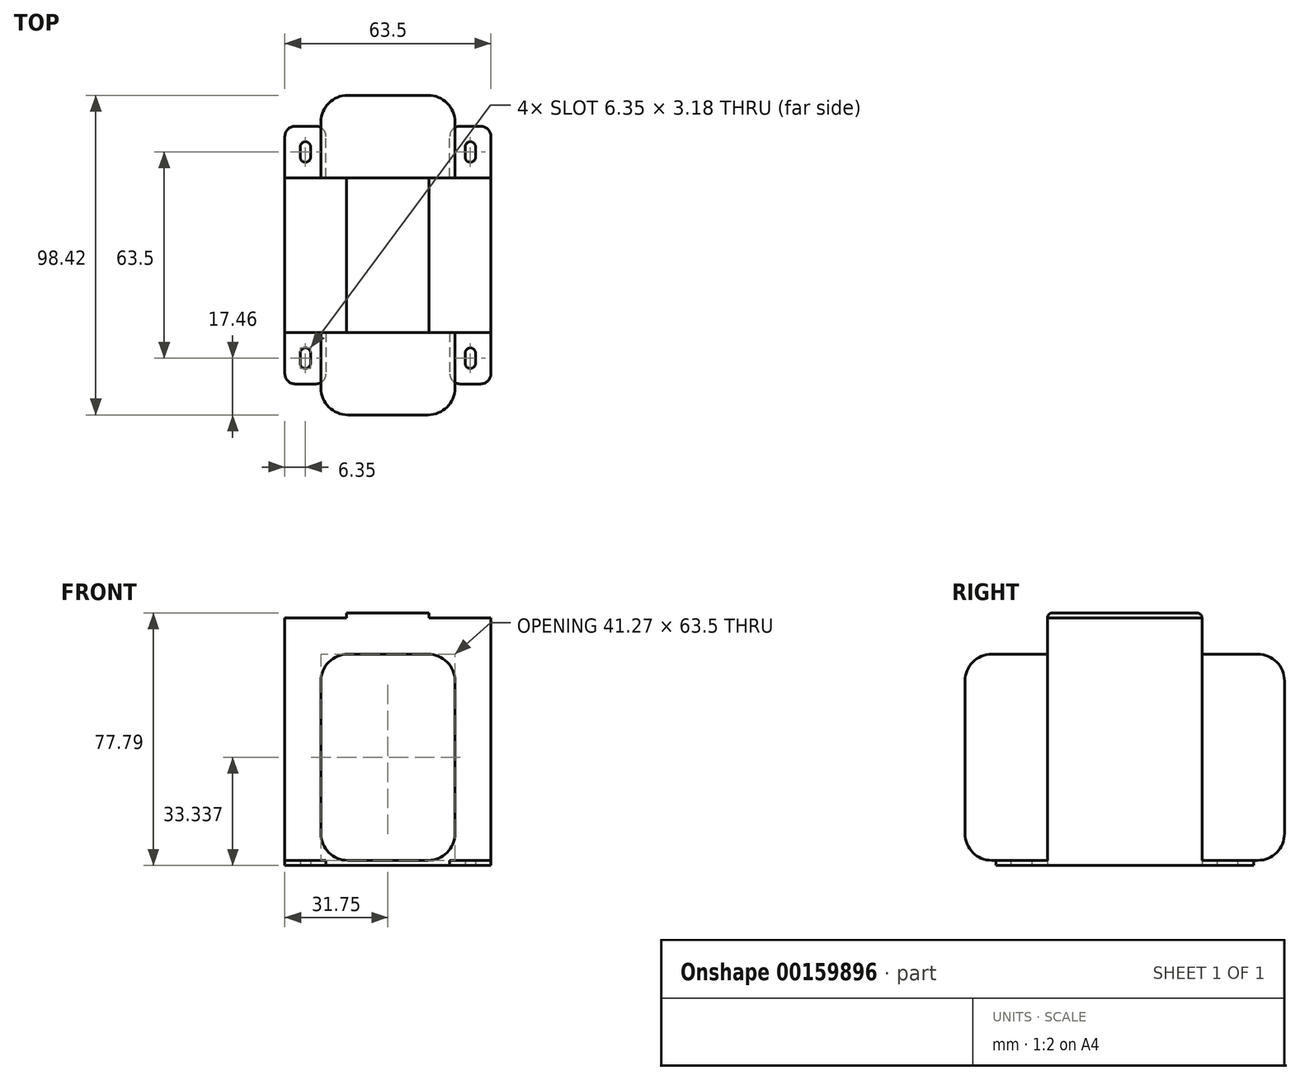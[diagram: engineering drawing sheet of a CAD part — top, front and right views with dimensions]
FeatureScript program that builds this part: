
annotation { "Feature Type Name" : "Feature", "Feature Type Description" : "" }
export const myFeature = defineFeature(function(context is Context, id is Id, definition is map)
    precondition{}
    {
        {
            var Q0;
            Q0=qCreatedBy(makeId("Top.planeOp"),FACE);
            var sketch = newSketch(context, id + "F0", { "sketchPlane" : qUnion([Q0])});
            skLineSegment(sketch, "E0.bottom", {"start": v(31.75, -23.81) * mm, "end": v(-31.75, -23.81) * mm});
            skLineSegment(sketch, "E0.top", {"start": v(31.75, 23.81) * mm, "end": v(-31.75, 23.81) * mm});
            skLineSegment(sketch, "E0.left", {"start": v(31.75, -23.81) * mm, "end": v(31.75, 23.81) * mm});
            skLineSegment(sketch, "E0.right", {"start": v(-31.75, -23.81) * mm, "end": v(-31.75, 23.81) * mm});
            skPoint(sketch, "E0.middle", {"position": v(0, 0) * mm});
            skSolve(sketch);
        }
        {
            var Q0;
            Q0=makeQuery(id+"F0.imprint","IMPRINT",FACE,{"disambiguationData":[TD([[makeQuery(id+"F0.imprint","IMPRINT",EDGE,{"derivedFrom":sQuery(id+"F0.wireOp",EDGE,"E0.bottom")}),-1.0]])]});
            extrude(context, id + "F1", {"entities" : qUnion([Q0]), "depth" : 76.2 * mm});
        }
        {
            var Q0;
            Q0=makeQuery(id+"F1.opExtrude","SWEPT_FACE",FACE,{"disambiguationData":[OSD([sQuery(id+"F0.wireOp",EDGE,"E0.bottom")])]});
            var sketch = newSketch(context, id + "F2", { "sketchPlane" : qUnion([Q0])});
            skLineSegment(sketch, "E1.bottom", {"start": v(-20.64, 65.09) * mm, "end": v(20.64, 65.09) * mm});
            skLineSegment(sketch, "E1.top", {"start": v(-20.64, 1.59) * mm, "end": v(20.64, 1.59) * mm});
            skLineSegment(sketch, "E1.left", {"start": v(-20.64, 65.09) * mm, "end": v(-20.64, 1.59) * mm});
            skLineSegment(sketch, "E1.right", {"start": v(20.64, 65.09) * mm, "end": v(20.64, 1.59) * mm});
            skSolve(sketch);
        }
        {
            var Q0;
            Q0=makeQuery(id+"F2.imprint","IMPRINT",FACE,{"disambiguationData":[TD([[makeQuery(id+"F2.imprint","IMPRINT",EDGE,{"derivedFrom":sQuery(id+"F2.wireOp",EDGE,"E1.bottom")}),-1.0]])]});
            extrude(context, id + "F3", {"entities" : qUnion([Q0]), "depth" : 25.4 * mm});
        }
        {
            var Q0;
            Q0=makeQuery(id+"F3.opExtrude","SWEPT_EDGE",EDGE,{"disambiguationData":[OSD([sQuery(id+"F2.wireOp",EDGE,"E1.bottom"),sQuery(id+"F2.wireOp",EDGE,"E1.left")])]});
            var Q1;
            Q1=makeQuery(id+"F3.opExtrude","SWEPT_EDGE",EDGE,{"disambiguationData":[OSD([sQuery(id+"F2.wireOp",EDGE,"E1.bottom"),sQuery(id+"F2.wireOp",EDGE,"E1.right")])]});
            var Q2;
            Q2=makeQuery(id+"F3.opExtrude","SWEPT_EDGE",EDGE,{"disambiguationData":[OSD([sQuery(id+"F0.wireOp",EDGE,"E0.bottom"),sQuery(id+"F2.wireOp",EDGE,"E1.top"),sQuery(id+"F2.wireOp",EDGE,"E1.left")])]});
            var Q3;
            Q3=makeQuery(id+"F3.opExtrude","SWEPT_EDGE",EDGE,{"disambiguationData":[OSD([sQuery(id+"F0.wireOp",EDGE,"E0.bottom"),sQuery(id+"F2.wireOp",EDGE,"E1.top"),sQuery(id+"F2.wireOp",EDGE,"E1.right")])]});
            var Q4;
            Q4=makeQuery(id+"F3.opExtrude","CAP_EDGE",EDGE,{"disambiguationData":[OSD([sQuery(id+"F2.wireOp",EDGE,"E1.right")])],"isStart":false});
            var Q5;
            Q5=makeQuery(id+"F3.opExtrude","CAP_FACE",FACE,{"disambiguationData":[OSD([sQuery(id+"F2.wireOp",EDGE,"E1.bottom"),sQuery(id+"F2.wireOp",EDGE,"E1.top"),sQuery(id+"F2.wireOp",EDGE,"E1.left"),sQuery(id+"F2.wireOp",EDGE,"E1.right")])],"isStart":false});
            fillet(context, id + "F4", {"entities" : qUnion([Q0, Q1, Q2, Q3, Q4, Q5]), "radius" : 8.25 * mm, "tangentPropagation" : true, "allowEdgeOverflow" : false});
        }
        {
            var Q0;
            Q0=makeQuery(id+"F3.opExtrude","SWEPT_BODY",BODY,{"disambiguationData":[OSD([sQuery(id+"F2.wireOp",EDGE,"E1.bottom"),sQuery(id+"F2.wireOp",EDGE,"E1.top"),sQuery(id+"F2.wireOp",EDGE,"E1.left"),sQuery(id+"F2.wireOp",EDGE,"E1.right")])]});
            var Q1;
            Q1=qCreatedBy(makeId("Front.planeOp"),FACE);
            mirror(context, id + "F5", {"operationType" : NewBodyOperationType.ADD, "entities" : qUnion([Q0]), "mirrorPlane" : qUnion([Q1])});
        }
        {
            var Q0;
            {var subQ0=makeQuery(id+"F3.opExtrude","SWEPT_FACE",FACE,{"disambiguationData":[OSD([sQuery(id+"F2.wireOp",EDGE,"E1.top")])]});Q0=makeQuery(id+"F5.boolean.opBoolean","MERGE",FACE,{"derivedFrom":[makeQuery(id+"F1.opExtrude","CAP_FACE",FACE,{"disambiguationData":[OSD([sQuery(id+"F0.wireOp",EDGE,"E0.bottom"),sQuery(id+"F0.wireOp",EDGE,"E0.top"),sQuery(id+"F0.wireOp",EDGE,"E0.left"),sQuery(id+"F0.wireOp",EDGE,"E0.right")])],"isStart":true}),subQ0,makeQuery(id+"F5.opPattern","COPY",FACE,{"derivedFrom":subQ0,"instanceName":"1"})]});}
            var sketch = newSketch(context, id + "F6", { "sketchPlane" : qUnion([Q0])});
            skLineSegment(sketch, "E2.bottom", {"start": v(-31.75, 23.81) * mm, "end": v(-19.05, 23.81) * mm});
            skLineSegment(sketch, "E2.top", {"start": v(-31.75, 39.69) * mm, "end": v(-19.05, 39.69) * mm});
            skLineSegment(sketch, "E2.left", {"start": v(-31.75, 23.81) * mm, "end": v(-31.75, 39.69) * mm});
            skLineSegment(sketch, "E2.right", {"start": v(-19.05, 23.81) * mm, "end": v(-19.05, 39.69) * mm});
            skLineSegment(sketch, "E3.MirrorCS", {"start": v(31.75, 23.81) * mm, "end": v(19.05, 23.81) * mm});
            skLineSegment(sketch, "E4.MirrorCS", {"start": v(19.05, 23.81) * mm, "end": v(19.05, 39.69) * mm});
            skLineSegment(sketch, "E5.MirrorCS", {"start": v(31.75, 23.81) * mm, "end": v(31.75, 39.69) * mm});
            skLineSegment(sketch, "E6.MirrorCS", {"start": v(31.75, 39.69) * mm, "end": v(19.05, 39.69) * mm});
            skLineSegment(sketch, "E7.MirrorCS", {"start": v(31.75, -23.81) * mm, "end": v(19.05, -23.81) * mm});
            skLineSegment(sketch, "E8.MirrorCS", {"start": v(31.75, -23.81) * mm, "end": v(31.75, -39.69) * mm});
            skLineSegment(sketch, "E9.MirrorCS", {"start": v(31.75, -39.69) * mm, "end": v(19.05, -39.69) * mm});
            skLineSegment(sketch, "E10.MirrorCS", {"start": v(19.05, -23.81) * mm, "end": v(19.05, -39.69) * mm});
            skLineSegment(sketch, "E11.MirrorCS", {"start": v(-31.75, -39.69) * mm, "end": v(-19.05, -39.69) * mm});
            skLineSegment(sketch, "E12.MirrorCS", {"start": v(-19.05, -23.81) * mm, "end": v(-19.05, -39.69) * mm});
            skLineSegment(sketch, "E13.MirrorCS", {"start": v(-31.75, -23.81) * mm, "end": v(-31.75, -39.69) * mm});
            skLineSegment(sketch, "E14.MirrorCS", {"start": v(-31.75, -23.81) * mm, "end": v(-19.05, -23.81) * mm});
            skSolve(sketch);
        }
        {
            var Q0;
            Q0=makeQuery(id+"F6.imprint","IMPRINT",FACE,{"disambiguationData":[TD([[makeQuery(id+"F6.imprint","IMPRINT",EDGE,{"derivedFrom":sQuery(id+"F6.wireOp",EDGE,"E2.bottom")}),-1.0]])]});
            var Q1;
            Q1=makeQuery(id+"F6.imprint","IMPRINT",FACE,{"disambiguationData":[TD([[makeQuery(id+"F6.imprint","IMPRINT",EDGE,{"derivedFrom":sQuery(id+"F6.wireOp",EDGE,"E3.MirrorCS")}),-1.0]])]});
            var Q2;
            Q2=makeQuery(id+"F6.imprint","IMPRINT",FACE,{"disambiguationData":[TD([[makeQuery(id+"F6.imprint","IMPRINT",EDGE,{"derivedFrom":sQuery(id+"F6.wireOp",EDGE,"E7.MirrorCS")}),1.0]])]});
            var Q3;
            Q3=makeQuery(id+"F6.imprint","IMPRINT",FACE,{"disambiguationData":[TD([[makeQuery(id+"F6.imprint","IMPRINT",EDGE,{"derivedFrom":sQuery(id+"F6.wireOp",EDGE,"E11.MirrorCS")}),1.0]])]});
            extrude(context, id + "F7", {"entities" : qUnion([Q0, Q1, Q2, Q3]), "operationType" : NewBodyOperationType.ADD, "oppositeDirection" : true, "depth" : 1.59 * mm});
        }
        {
            var Q0;
            Q0=makeQuery(id+"F7.opExtrude","SWEPT_EDGE",EDGE,{"disambiguationData":[OSD([sQuery(id+"F6.wireOp",EDGE,"E2.top"),sQuery(id+"F6.wireOp",EDGE,"E2.left")])]});
            var Q1;
            Q1=makeQuery(id+"F7.opExtrude","SWEPT_EDGE",EDGE,{"disambiguationData":[OSD([sQuery(id+"F6.wireOp",EDGE,"E2.top"),sQuery(id+"F6.wireOp",EDGE,"E2.right")])]});
            var Q2;
            Q2=makeQuery(id+"F7.opExtrude","SWEPT_EDGE",EDGE,{"disambiguationData":[OSD([sQuery(id+"F6.wireOp",EDGE,"E4.MirrorCS"),sQuery(id+"F6.wireOp",EDGE,"E6.MirrorCS")])]});
            var Q3;
            Q3=makeQuery(id+"F7.opExtrude","SWEPT_EDGE",EDGE,{"disambiguationData":[OSD([sQuery(id+"F6.wireOp",EDGE,"E5.MirrorCS"),sQuery(id+"F6.wireOp",EDGE,"E6.MirrorCS")])]});
            var Q4;
            Q4=makeQuery(id+"F7.opExtrude","SWEPT_EDGE",EDGE,{"disambiguationData":[OSD([sQuery(id+"F6.wireOp",EDGE,"E8.MirrorCS"),sQuery(id+"F6.wireOp",EDGE,"E9.MirrorCS")])]});
            var Q5;
            Q5=makeQuery(id+"F7.opExtrude","SWEPT_EDGE",EDGE,{"disambiguationData":[OSD([sQuery(id+"F6.wireOp",EDGE,"E9.MirrorCS"),sQuery(id+"F6.wireOp",EDGE,"E10.MirrorCS")])]});
            var Q6;
            Q6=makeQuery(id+"F7.opExtrude","SWEPT_EDGE",EDGE,{"disambiguationData":[OSD([sQuery(id+"F6.wireOp",EDGE,"E11.MirrorCS"),sQuery(id+"F6.wireOp",EDGE,"E12.MirrorCS")])]});
            var Q7;
            Q7=makeQuery(id+"F7.opExtrude","SWEPT_EDGE",EDGE,{"disambiguationData":[OSD([sQuery(id+"F6.wireOp",EDGE,"E11.MirrorCS"),sQuery(id+"F6.wireOp",EDGE,"E13.MirrorCS")])]});
            fillet(context, id + "F8", {"entities" : qUnion([Q0, Q1, Q2, Q3, Q4, Q5, Q6, Q7]), "radius" : 3.17 * mm, "tangentPropagation" : true, "allowEdgeOverflow" : false});
        }
        {
            var Q0;
            Q0=makeQuery(id+"F7.boolean.opBoolean","MERGE",FACE,{"derivedFrom":[makeQuery(id+"F1.opExtrude","CAP_FACE",FACE,{"disambiguationData":[OSD([sQuery(id+"F0.wireOp",EDGE,"E0.bottom"),sQuery(id+"F0.wireOp",EDGE,"E0.top"),sQuery(id+"F0.wireOp",EDGE,"E0.left"),sQuery(id+"F0.wireOp",EDGE,"E0.right")])],"isStart":true}),makeQuery(id+"F7.opExtrude","CAP_FACE",FACE,{"disambiguationData":[OSD([sQuery(id+"F6.wireOp",EDGE,"E2.bottom"),sQuery(id+"F6.wireOp",EDGE,"E2.top"),sQuery(id+"F6.wireOp",EDGE,"E2.left"),sQuery(id+"F6.wireOp",EDGE,"E2.right")])],"isStart":true}),makeQuery(id+"F7.opExtrude","CAP_FACE",FACE,{"disambiguationData":[OSD([sQuery(id+"F6.wireOp",EDGE,"E3.MirrorCS"),sQuery(id+"F6.wireOp",EDGE,"E4.MirrorCS"),sQuery(id+"F6.wireOp",EDGE,"E5.MirrorCS"),sQuery(id+"F6.wireOp",EDGE,"E6.MirrorCS")])],"isStart":true}),makeQuery(id+"F7.opExtrude","CAP_FACE",FACE,{"disambiguationData":[OSD([sQuery(id+"F6.wireOp",EDGE,"E7.MirrorCS"),sQuery(id+"F6.wireOp",EDGE,"E8.MirrorCS"),sQuery(id+"F6.wireOp",EDGE,"E9.MirrorCS"),sQuery(id+"F6.wireOp",EDGE,"E10.MirrorCS")])],"isStart":true}),makeQuery(id+"F7.opExtrude","CAP_FACE",FACE,{"disambiguationData":[OSD([sQuery(id+"F6.wireOp",EDGE,"E11.MirrorCS"),sQuery(id+"F6.wireOp",EDGE,"E12.MirrorCS"),sQuery(id+"F6.wireOp",EDGE,"E13.MirrorCS"),sQuery(id+"F6.wireOp",EDGE,"E14.MirrorCS")])],"isStart":true})]});
            var sketch = newSketch(context, id + "F9", { "sketchPlane" : qUnion([Q0])});
            skLineSegment(sketch, "E15", {"start": v(-25.4, 39.69) * mm, "end": v(-25.4, 23.81) * mm, "construction": true});
            skLineSegment(sketch, "E16", {"start": v(-31.75, 31.75) * mm, "end": v(-19.05, 31.75) * mm, "construction": true});
            skPoint(sketch, "E16.startSnap0", {"position": v(-25.4, 31.75) * mm});
            skLineSegment(sketch, "E17.bottom", {"start": v(-26.99, 28.58) * mm, "end": v(-23.81, 28.58) * mm});
            skLineSegment(sketch, "E17.top", {"start": v(-26.99, 34.93) * mm, "end": v(-23.81, 34.93) * mm});
            skLineSegment(sketch, "E17.left", {"start": v(-26.99, 28.58) * mm, "end": v(-26.99, 34.93) * mm});
            skLineSegment(sketch, "E17.right", {"start": v(-23.81, 28.58) * mm, "end": v(-23.81, 34.93) * mm});
            skLineSegment(sketch, "E18.MirrorCS", {"start": v(26.99, 34.93) * mm, "end": v(23.81, 34.93) * mm});
            skLineSegment(sketch, "E19.MirrorCS", {"start": v(23.81, 28.58) * mm, "end": v(23.81, 34.93) * mm});
            skLineSegment(sketch, "E20.MirrorCS", {"start": v(26.99, 28.58) * mm, "end": v(26.99, 34.93) * mm});
            skLineSegment(sketch, "E21.MirrorCS", {"start": v(26.99, 28.58) * mm, "end": v(23.81, 28.58) * mm});
            skLineSegment(sketch, "E22.MirrorCS", {"start": v(26.99, -28.58) * mm, "end": v(23.81, -28.58) * mm});
            skLineSegment(sketch, "E23.MirrorCS", {"start": v(26.99, -28.58) * mm, "end": v(26.99, -34.93) * mm});
            skLineSegment(sketch, "E24.MirrorCS", {"start": v(26.99, -34.93) * mm, "end": v(23.81, -34.93) * mm});
            skLineSegment(sketch, "E25.MirrorCS", {"start": v(23.81, -28.58) * mm, "end": v(23.81, -34.93) * mm});
            skLineSegment(sketch, "E26.MirrorCS", {"start": v(-26.99, -28.58) * mm, "end": v(-23.81, -28.58) * mm});
            skLineSegment(sketch, "E27.MirrorCS", {"start": v(-26.99, -34.93) * mm, "end": v(-23.81, -34.93) * mm});
            skLineSegment(sketch, "E28.MirrorCS", {"start": v(-26.99, -28.58) * mm, "end": v(-26.99, -34.93) * mm});
            skLineSegment(sketch, "E29.MirrorCS", {"start": v(-23.81, -28.58) * mm, "end": v(-23.81, -34.93) * mm});
            skSolve(sketch);
        }
        {
            var Q0;
            Q0=makeQuery(id+"F9.imprint","IMPRINT",FACE,{"disambiguationData":[TD([[makeQuery(id+"F9.imprint","IMPRINT",EDGE,{"derivedFrom":sQuery(id+"F9.wireOp",EDGE,"E17.bottom")}),1.0]])]});
            var Q1;
            Q1=makeQuery(id+"F9.imprint","IMPRINT",FACE,{"disambiguationData":[TD([[makeQuery(id+"F9.imprint","IMPRINT",EDGE,{"derivedFrom":sQuery(id+"F9.wireOp",EDGE,"E18.MirrorCS")}),1.0]])]});
            var Q2;
            Q2=makeQuery(id+"F9.imprint","IMPRINT",FACE,{"disambiguationData":[TD([[makeQuery(id+"F9.imprint","IMPRINT",EDGE,{"derivedFrom":sQuery(id+"F9.wireOp",EDGE,"E22.MirrorCS")}),1.0]])]});
            var Q3;
            Q3=makeQuery(id+"F9.imprint","IMPRINT",FACE,{"disambiguationData":[TD([[makeQuery(id+"F9.imprint","IMPRINT",EDGE,{"derivedFrom":sQuery(id+"F9.wireOp",EDGE,"E26.MirrorCS")}),-1.0]])]});
            extrude(context, id + "F10", {"entities" : qUnion([Q0, Q1, Q2, Q3]), "operationType" : NewBodyOperationType.REMOVE, "oppositeDirection" : true, "depth" : 25.4 * mm});
        }
        {
            var Q0;
            Q0=makeQuery(id+"F10.boolean.opBoolean","COPY",EDGE,{"derivedFrom":makeQuery(id+"F10.opExtrude","SWEPT_EDGE",EDGE,{"disambiguationData":[OSD([sQuery(id+"F9.wireOp",EDGE,"E17.top"),sQuery(id+"F9.wireOp",EDGE,"E17.left")])]})});
            var Q1;
            Q1=makeQuery(id+"F10.boolean.opBoolean","COPY",EDGE,{"derivedFrom":makeQuery(id+"F10.opExtrude","SWEPT_EDGE",EDGE,{"disambiguationData":[OSD([sQuery(id+"F9.wireOp",EDGE,"E17.top"),sQuery(id+"F9.wireOp",EDGE,"E17.right")])]})});
            var Q2;
            Q2=makeQuery(id+"F10.boolean.opBoolean","COPY",EDGE,{"derivedFrom":makeQuery(id+"F10.opExtrude","SWEPT_EDGE",EDGE,{"disambiguationData":[OSD([sQuery(id+"F9.wireOp",EDGE,"E17.bottom"),sQuery(id+"F9.wireOp",EDGE,"E17.left")])]})});
            var Q3;
            Q3=makeQuery(id+"F10.boolean.opBoolean","COPY",EDGE,{"derivedFrom":makeQuery(id+"F10.opExtrude","SWEPT_EDGE",EDGE,{"disambiguationData":[OSD([sQuery(id+"F9.wireOp",EDGE,"E17.bottom"),sQuery(id+"F9.wireOp",EDGE,"E17.right")])]})});
            var Q4;
            Q4=makeQuery(id+"F10.boolean.opBoolean","COPY",EDGE,{"derivedFrom":makeQuery(id+"F10.opExtrude","SWEPT_EDGE",EDGE,{"disambiguationData":[OSD([sQuery(id+"F9.wireOp",EDGE,"E21.MirrorCS"),sQuery(id+"F9.wireOp",EDGE,"E20.MirrorCS")])]})});
            var Q5;
            Q5=makeQuery(id+"F10.boolean.opBoolean","COPY",EDGE,{"derivedFrom":makeQuery(id+"F10.opExtrude","SWEPT_EDGE",EDGE,{"disambiguationData":[OSD([sQuery(id+"F9.wireOp",EDGE,"E18.MirrorCS"),sQuery(id+"F9.wireOp",EDGE,"E20.MirrorCS")])]})});
            var Q6;
            Q6=makeQuery(id+"F10.boolean.opBoolean","COPY",EDGE,{"derivedFrom":makeQuery(id+"F10.opExtrude","SWEPT_EDGE",EDGE,{"disambiguationData":[OSD([sQuery(id+"F9.wireOp",EDGE,"E18.MirrorCS"),sQuery(id+"F9.wireOp",EDGE,"E19.MirrorCS")])]})});
            var Q7;
            Q7=makeQuery(id+"F10.boolean.opBoolean","COPY",EDGE,{"derivedFrom":makeQuery(id+"F10.opExtrude","SWEPT_EDGE",EDGE,{"disambiguationData":[OSD([sQuery(id+"F9.wireOp",EDGE,"E19.MirrorCS"),sQuery(id+"F9.wireOp",EDGE,"E21.MirrorCS")])]})});
            var Q8;
            Q8=makeQuery(id+"F10.boolean.opBoolean","COPY",EDGE,{"derivedFrom":makeQuery(id+"F10.opExtrude","SWEPT_EDGE",EDGE,{"disambiguationData":[OSD([sQuery(id+"F9.wireOp",EDGE,"E27.MirrorCS"),sQuery(id+"F9.wireOp",EDGE,"E28.MirrorCS")])]})});
            var Q9;
            Q9=makeQuery(id+"F10.boolean.opBoolean","COPY",EDGE,{"derivedFrom":makeQuery(id+"F10.opExtrude","SWEPT_EDGE",EDGE,{"disambiguationData":[OSD([sQuery(id+"F9.wireOp",EDGE,"E27.MirrorCS"),sQuery(id+"F9.wireOp",EDGE,"E29.MirrorCS")])]})});
            var Q10;
            Q10=makeQuery(id+"F10.boolean.opBoolean","COPY",EDGE,{"derivedFrom":makeQuery(id+"F10.opExtrude","SWEPT_EDGE",EDGE,{"disambiguationData":[OSD([sQuery(id+"F9.wireOp",EDGE,"E26.MirrorCS"),sQuery(id+"F9.wireOp",EDGE,"E29.MirrorCS")])]})});
            var Q11;
            Q11=makeQuery(id+"F10.boolean.opBoolean","COPY",EDGE,{"derivedFrom":makeQuery(id+"F10.opExtrude","SWEPT_EDGE",EDGE,{"disambiguationData":[OSD([sQuery(id+"F9.wireOp",EDGE,"E26.MirrorCS"),sQuery(id+"F9.wireOp",EDGE,"E28.MirrorCS")])]})});
            var Q12;
            Q12=makeQuery(id+"F10.boolean.opBoolean","COPY",EDGE,{"derivedFrom":makeQuery(id+"F10.opExtrude","SWEPT_EDGE",EDGE,{"disambiguationData":[OSD([sQuery(id+"F9.wireOp",EDGE,"E22.MirrorCS"),sQuery(id+"F9.wireOp",EDGE,"E25.MirrorCS")])]})});
            var Q13;
            Q13=makeQuery(id+"F10.boolean.opBoolean","COPY",EDGE,{"derivedFrom":makeQuery(id+"F10.opExtrude","SWEPT_EDGE",EDGE,{"disambiguationData":[OSD([sQuery(id+"F9.wireOp",EDGE,"E23.MirrorCS"),sQuery(id+"F9.wireOp",EDGE,"E24.MirrorCS")])]})});
            var Q14;
            Q14=makeQuery(id+"F10.boolean.opBoolean","COPY",EDGE,{"derivedFrom":makeQuery(id+"F10.opExtrude","SWEPT_EDGE",EDGE,{"disambiguationData":[OSD([sQuery(id+"F9.wireOp",EDGE,"E24.MirrorCS"),sQuery(id+"F9.wireOp",EDGE,"E25.MirrorCS")])]})});
            var Q15;
            Q15=makeQuery(id+"F10.boolean.opBoolean","COPY",EDGE,{"derivedFrom":makeQuery(id+"F10.opExtrude","SWEPT_EDGE",EDGE,{"disambiguationData":[OSD([sQuery(id+"F9.wireOp",EDGE,"E22.MirrorCS"),sQuery(id+"F9.wireOp",EDGE,"E23.MirrorCS")])]})});
            fillet(context, id + "F11", {"entities" : qUnion([Q0, Q1, Q2, Q3, Q4, Q5, Q6, Q7, Q8, Q9, Q10, Q11, Q12, Q13, Q14, Q15]), "radius" : 1.59 * mm, "tangentPropagation" : true, "allowEdgeOverflow" : false});
        }
        {
            var Q0;
            Q0=makeQuery(id+"F1.opExtrude","CAP_FACE",FACE,{"disambiguationData":[OSD([sQuery(id+"F0.wireOp",EDGE,"E0.bottom"),sQuery(id+"F0.wireOp",EDGE,"E0.top"),sQuery(id+"F0.wireOp",EDGE,"E0.left"),sQuery(id+"F0.wireOp",EDGE,"E0.right")])],"isStart":false});
            var sketch = newSketch(context, id + "F12", { "sketchPlane" : qUnion([Q0])});
            skLineSegment(sketch, "E30.bottom", {"start": v(12.7, -23.81) * mm, "end": v(-12.7, -23.81) * mm});
            skLineSegment(sketch, "E30.top", {"start": v(12.7, 23.81) * mm, "end": v(-12.7, 23.81) * mm});
            skLineSegment(sketch, "E30.left", {"start": v(12.7, -23.81) * mm, "end": v(12.7, 23.81) * mm});
            skLineSegment(sketch, "E30.right", {"start": v(-12.7, -23.81) * mm, "end": v(-12.7, 23.81) * mm});
            skPoint(sketch, "E30.middle", {"position": v(0, 0) * mm});
            skSolve(sketch);
        }
        {
            var Q0;
            Q0=makeQuery(id+"F12.imprint","IMPRINT",FACE,{"disambiguationData":[TD([[makeQuery(id+"F12.imprint","IMPRINT",EDGE,{"derivedFrom":sQuery(id+"F12.wireOp",EDGE,"E30.bottom")}),-1.0]])]});
            extrude(context, id + "F13", {"entities" : qUnion([Q0]), "operationType" : NewBodyOperationType.ADD, "depth" : 1.59 * mm});
        }
        {
            var Q0;
            Q0=makeQuery(id+"F13.opExtrude","CAP_EDGE",EDGE,{"disambiguationData":[OSD([sQuery(id+"F12.wireOp",EDGE,"E30.bottom")])],"isStart":false});
            var Q1;
            Q1=makeQuery(id+"F13.opExtrude","CAP_EDGE",EDGE,{"disambiguationData":[OSD([sQuery(id+"F12.wireOp",EDGE,"E30.top")])],"isStart":false});
            fillet(context, id + "F14", {"entities" : qUnion([Q0, Q1]), "radius" : 1.59 * mm, "tangentPropagation" : true, "allowEdgeOverflow" : false});
        }
    });
